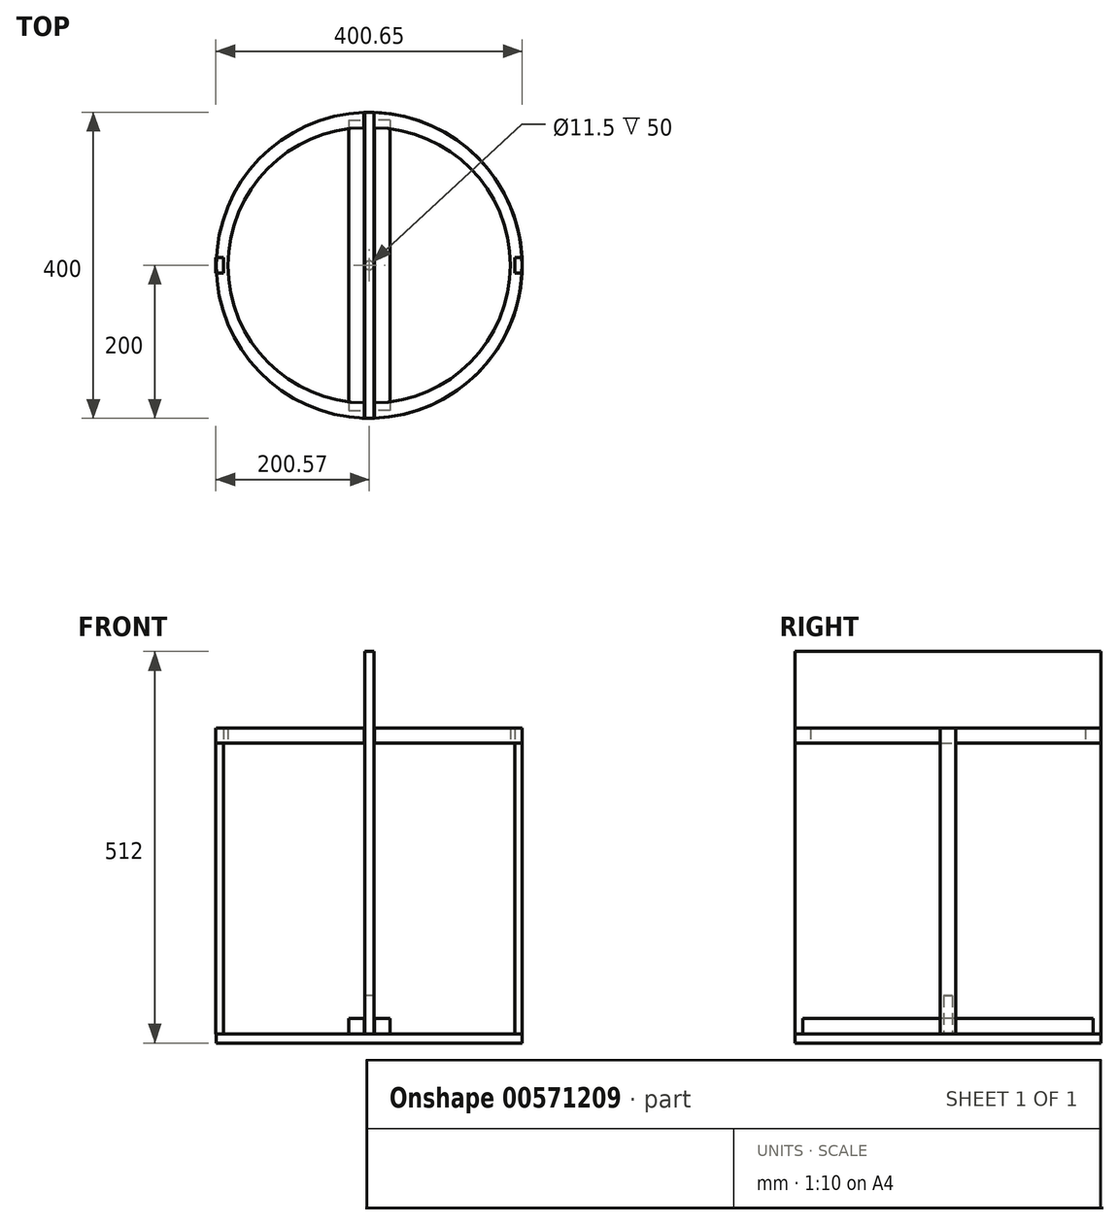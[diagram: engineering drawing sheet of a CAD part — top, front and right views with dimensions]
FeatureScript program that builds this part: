
annotation { "Feature Type Name" : "Feature", "Feature Type Description" : "" }
export const myFeature = defineFeature(function(context is Context, id is Id, definition is map)
    precondition{}
    {
        {
            var Q0;
            Q0=qCreatedBy(makeId("Top.planeOp"),FACE);
            var sketch = newSketch(context, id + "F0", { "sketchPlane" : qUnion([Q0])});
            skCircle(sketch, "E0", {"center": v(0, 0) * mm, "radius": 200 * mm});
            skSolve(sketch);
        }
        {
            var Q0;
            Q0 = qSketchRegion(id + "F0", true);
            extrude(context, id + "F1", {"entities" : qUnion([Q0]), "oppositeDirection" : true, "depth" : 12 * mm, "offsetDistance" : 25.4 * mm});
        }
        {
            var Q0;
            Q0=qCreatedBy(makeId("Top.planeOp"),FACE);
            var sketch = newSketch(context, id + "F2", { "sketchPlane" : qUnion([Q0])});
            skLineSegment(sketch, "E1.bottom", {"start": v(-6, 200) * mm, "end": v(6, 200) * mm});
            skLineSegment(sketch, "E1.top", {"start": v(-6, -200) * mm, "end": v(6, -200) * mm});
            skLineSegment(sketch, "E1.left", {"start": v(-6, 200) * mm, "end": v(-6, -200) * mm});
            skLineSegment(sketch, "E1.right", {"start": v(6, 200) * mm, "end": v(6, -200) * mm});
            skPoint(sketch, "E1.middle", {"position": v(0, 0) * mm});
            skSolve(sketch);
        }
        {
            var Q0;
            Q0 = qSketchRegion(id + "F2", true);
            extrude(context, id + "F3", {"entities" : qUnion([Q0]), "depth" : 500 * mm, "offsetDistance" : 25.4 * mm});
        }
        {
            var Q0;
            Q0=qCreatedBy(makeId("Top.planeOp"),FACE);
            var sketch = newSketch(context, id + "F4", { "sketchPlane" : qUnion([Q0])});
            skLineSegment(sketch, "E2.bottom", {"start": v(-26.58, 190) * mm, "end": v(-6.58, 190) * mm});
            skLineSegment(sketch, "E2.top", {"start": v(-26.58, -190) * mm, "end": v(-6.58, -190) * mm});
            skLineSegment(sketch, "E2.left", {"start": v(-26.58, 190) * mm, "end": v(-26.58, -190) * mm});
            skLineSegment(sketch, "E2.right", {"start": v(-6.58, 190) * mm, "end": v(-6.58, -190) * mm});
            skPoint(sketch, "E2.middle", {"position": v(-16.58, 0) * mm});
            skSolve(sketch);
        }
        {
            var Q0;
            Q0 = qSketchRegion(id + "F4", true);
            extrude(context, id + "F5", {"entities" : qUnion([Q0]), "depth" : 20 * mm, "offsetDistance" : 25.4 * mm});
        }
        {
            var Q0;
            Q0=qCreatedBy(makeId("Top.planeOp"),FACE);
            var sketch = newSketch(context, id + "F6", { "sketchPlane" : qUnion([Q0])});
            skLineSegment(sketch, "E3.bottom", {"start": v(26.9, 190) * mm, "end": v(6.9, 190) * mm});
            skLineSegment(sketch, "E3.top", {"start": v(26.9, -190) * mm, "end": v(6.9, -190) * mm});
            skLineSegment(sketch, "E3.left", {"start": v(26.9, 190) * mm, "end": v(26.9, -190) * mm});
            skLineSegment(sketch, "E3.right", {"start": v(6.9, 190) * mm, "end": v(6.9, -190) * mm});
            skPoint(sketch, "E3.middle", {"position": v(16.9, 0) * mm});
            skSolve(sketch);
        }
        {
            var Q0;
            Q0 = qSketchRegion(id + "F6", true);
            extrude(context, id + "F7", {"entities" : qUnion([Q0]), "depth" : 20 * mm, "offsetDistance" : 25.4 * mm});
        }
        {
            var Q0;
            Q0=qCreatedBy(makeId("Top.planeOp"),FACE);
            var sketch = newSketch(context, id + "F8", { "sketchPlane" : qUnion([Q0])});
            skLineSegment(sketch, "E4", {"start": v(-6.88, 179.9) * mm, "end": v(-6.88, 199.9) * mm});
            skArc(sketch, "E5", {"start": v(-6.88, 199.9) * mm, "mid": v(-200.19, -0.28) * mm, "end": v(-6.3, -199.9) * mm});
            skPoint(sketch, "E6", {"position": v(-200.19, -0.28) * mm});
            skLineSegment(sketch, "E7", {"start": v(-6.3, -199.9) * mm, "end": v(-6.3, -179.9) * mm});
            skArc(sketch, "E8", {"start": v(-6.88, 179.9) * mm, "mid": v(-184.8, -0.28) * mm, "end": v(-6.3, -179.9) * mm});
            skSolve(sketch);
        }
        {
            var Q0;
            Q0 = qSketchRegion(id + "F8", true);
            extrude(context, id + "F9", {"entities" : qUnion([Q0]), "depth" : 20 * mm, "offsetDistance" : 25.4 * mm});
        }
        {
            var Q0;
            Q0=makeQuery(id+"F9.opExtrude","SWEPT_BODY",BODY,{"disambiguationData":[OSD([sQuery(id+"F8.wireOp",EDGE,"E4"),sQuery(id+"F8.wireOp",EDGE,"E5"),sQuery(id+"F8.wireOp",EDGE,"E7"),sQuery(id+"F8.wireOp",EDGE,"E8")])]});
            transform(context, id + "F10", {"entities" : qUnion([Q0]), "transformType" : TransformType.TRANSLATION_3D, "dx" : 0 * mm, "dy" : 0 * mm, "dz" : 380 * mm, "makeCopy" : true});
        }
        {
            var Q0;
            Q0=makeQuery(id+"F9.opExtrude","SWEPT_BODY",BODY,{"disambiguationData":[OSD([sQuery(id+"F8.wireOp",EDGE,"E4"),sQuery(id+"F8.wireOp",EDGE,"E5"),sQuery(id+"F8.wireOp",EDGE,"E7"),sQuery(id+"F8.wireOp",EDGE,"E8")])]});
            deleteBodies(context, id + "F11", {"entities" : qUnion([Q0])});
        }
        {
            var Q0;
            Q0=makeQuery(id+"F10.opPattern","COPY",BODY,{"derivedFrom":makeQuery(id+"F9.opExtrude","SWEPT_BODY",BODY,{"disambiguationData":[OSD([sQuery(id+"F8.wireOp",EDGE,"E4"),sQuery(id+"F8.wireOp",EDGE,"E5"),sQuery(id+"F8.wireOp",EDGE,"E7"),sQuery(id+"F8.wireOp",EDGE,"E8")])]}),"instanceName":"1"});
            var Q1;
            Q1=makeQuery(id+"F10.opPattern","COPY",FACE,{"derivedFrom":makeQuery(id+"F9.opExtrude","SWEPT_FACE",FACE,{"disambiguationData":[OSD([sQuery(id+"F8.wireOp",EDGE,"E5")])]}),"instanceName":"1"});
            transform(context, id + "F12", {"entities" : qUnion([Q0]), "transformType" : TransformType.ROTATION, "transformAxis" : qUnion([Q1]), "angle" : 180 * degree, "makeCopy" : true});
        }
        {
            var Q0;
            Q0=qCreatedBy(makeId("Top.planeOp"),FACE);
            var sketch = newSketch(context, id + "F13", { "sketchPlane" : qUnion([Q0])});
            skLineSegment(sketch, "E9.bottom", {"start": v(-197.92, 10) * mm, "end": v(-187.92, 10) * mm});
            skLineSegment(sketch, "E9.top", {"start": v(-197.92, -10) * mm, "end": v(-187.92, -10) * mm});
            skLineSegment(sketch, "E9.left", {"start": v(-197.92, 10) * mm, "end": v(-197.92, -10) * mm});
            skLineSegment(sketch, "E9.right", {"start": v(-187.92, 10) * mm, "end": v(-187.92, -10) * mm});
            skPoint(sketch, "E9.middle", {"position": v(-192.92, 0) * mm});
            skPoint(sketch, "E10.middle", {"position": v(55.3, 0) * mm});
            skSolve(sketch);
        }
        {
            var Q0;
            Q0 = qSketchRegion(id + "F13", true);
            extrude(context, id + "F14", {"entities" : qUnion([Q0]), "depth" : 400 * mm, "offsetDistance" : 25.4 * mm});
        }
        {
            var Q0;
            Q0=makeQuery(id+"F14.opExtrude","SWEPT_BODY",BODY,{"disambiguationData":[OSD([sQuery(id+"F13.wireOp",EDGE,"E9.bottom"),sQuery(id+"F13.wireOp",EDGE,"E9.top"),sQuery(id+"F13.wireOp",EDGE,"E9.left"),sQuery(id+"F13.wireOp",EDGE,"E9.right")])]});
            transform(context, id + "F15", {"entities" : qUnion([Q0]), "transformType" : TransformType.TRANSLATION_3D, "dx" : 388 * mm, "dy" : 0 * mm, "dz" : 0 * mm, "makeCopy" : true});
        }
        {
            var Q0;
            Q0=makeQuery(id+"F14.opExtrude","SWEPT_BODY",BODY,{"disambiguationData":[OSD([sQuery(id+"F13.wireOp",EDGE,"E9.bottom"),sQuery(id+"F13.wireOp",EDGE,"E9.top"),sQuery(id+"F13.wireOp",EDGE,"E9.left"),sQuery(id+"F13.wireOp",EDGE,"E9.right")])]});
            deleteBodies(context, id + "F16", {"entities" : qUnion([Q0])});
        }
        {
            var Q0;
            Q0=makeQuery(id+"F15.opPattern","COPY",BODY,{"derivedFrom":makeQuery(id+"F14.opExtrude","SWEPT_BODY",BODY,{"disambiguationData":[OSD([sQuery(id+"F13.wireOp",EDGE,"E9.bottom"),sQuery(id+"F13.wireOp",EDGE,"E9.top"),sQuery(id+"F13.wireOp",EDGE,"E9.left"),sQuery(id+"F13.wireOp",EDGE,"E9.right")])]}),"instanceName":"1"});
            transform(context, id + "F17", {"entities" : qUnion([Q0]), "transformType" : TransformType.TRANSLATION_3D, "dx" : -390.14 * mm, "dy" : 0 * mm, "dz" : 0 * mm, "makeCopy" : true});
        }
        {
            var Q0;
            Q0=makeQuery(id+"F17.opPattern","COPY",BODY,{"derivedFrom":makeQuery(id+"F15.opPattern","COPY",BODY,{"derivedFrom":makeQuery(id+"F14.opExtrude","SWEPT_BODY",BODY,{"disambiguationData":[OSD([sQuery(id+"F13.wireOp",EDGE,"E9.bottom"),sQuery(id+"F13.wireOp",EDGE,"E9.top"),sQuery(id+"F13.wireOp",EDGE,"E9.left"),sQuery(id+"F13.wireOp",EDGE,"E9.right")])]}),"instanceName":"1"}),"instanceName":"1"});
            deleteBodies(context, id + "F18", {"entities" : qUnion([Q0])});
        }
        {
            var Q0;
            Q0=makeQuery(id+"F15.opPattern","COPY",BODY,{"derivedFrom":makeQuery(id+"F14.opExtrude","SWEPT_BODY",BODY,{"disambiguationData":[OSD([sQuery(id+"F13.wireOp",EDGE,"E9.bottom"),sQuery(id+"F13.wireOp",EDGE,"E9.top"),sQuery(id+"F13.wireOp",EDGE,"E9.left"),sQuery(id+"F13.wireOp",EDGE,"E9.right")])]}),"instanceName":"1"});
            transform(context, id + "F19", {"entities" : qUnion([Q0]), "transformType" : TransformType.TRANSLATION_3D, "dx" : -390.65 * mm, "dy" : 0 * mm, "dz" : 0 * mm, "makeCopy" : true});
        }
        {
            var Q0;
            Q0=qCreatedBy(makeId("Top.planeOp"),FACE);
            var sketch = newSketch(context, id + "F20", { "sketchPlane" : qUnion([Q0])});
            skCircle(sketch, "E11", {"center": v(0, 0) * mm, "radius": 5.75 * mm});
            skSolve(sketch);
        }
        {
            var Q0;
            Q0 = qSketchRegion(id + "F20", true);
            extrude(context, id + "F21", {"entities" : qUnion([Q0]), "operationType" : NewBodyOperationType.REMOVE, "depth" : 50 * mm, "offsetDistance" : 25.4 * mm});
        }
        {
            var Q0;
            Q0=makeQuery(id+"F1.opExtrude","SWEPT_BODY",BODY,{"disambiguationData":[OSD([sQuery(id+"F0.wireOp",EDGE,"E0")])]});
            transform(context, id + "F22", {"entities" : qUnion([Q0]), "transformType" : TransformType.TRANSLATION_3D, "dx" : 0 * mm, "dy" : 0 * mm, "dz" : 0 * mm, "makeCopy" : true});
        }
    });
